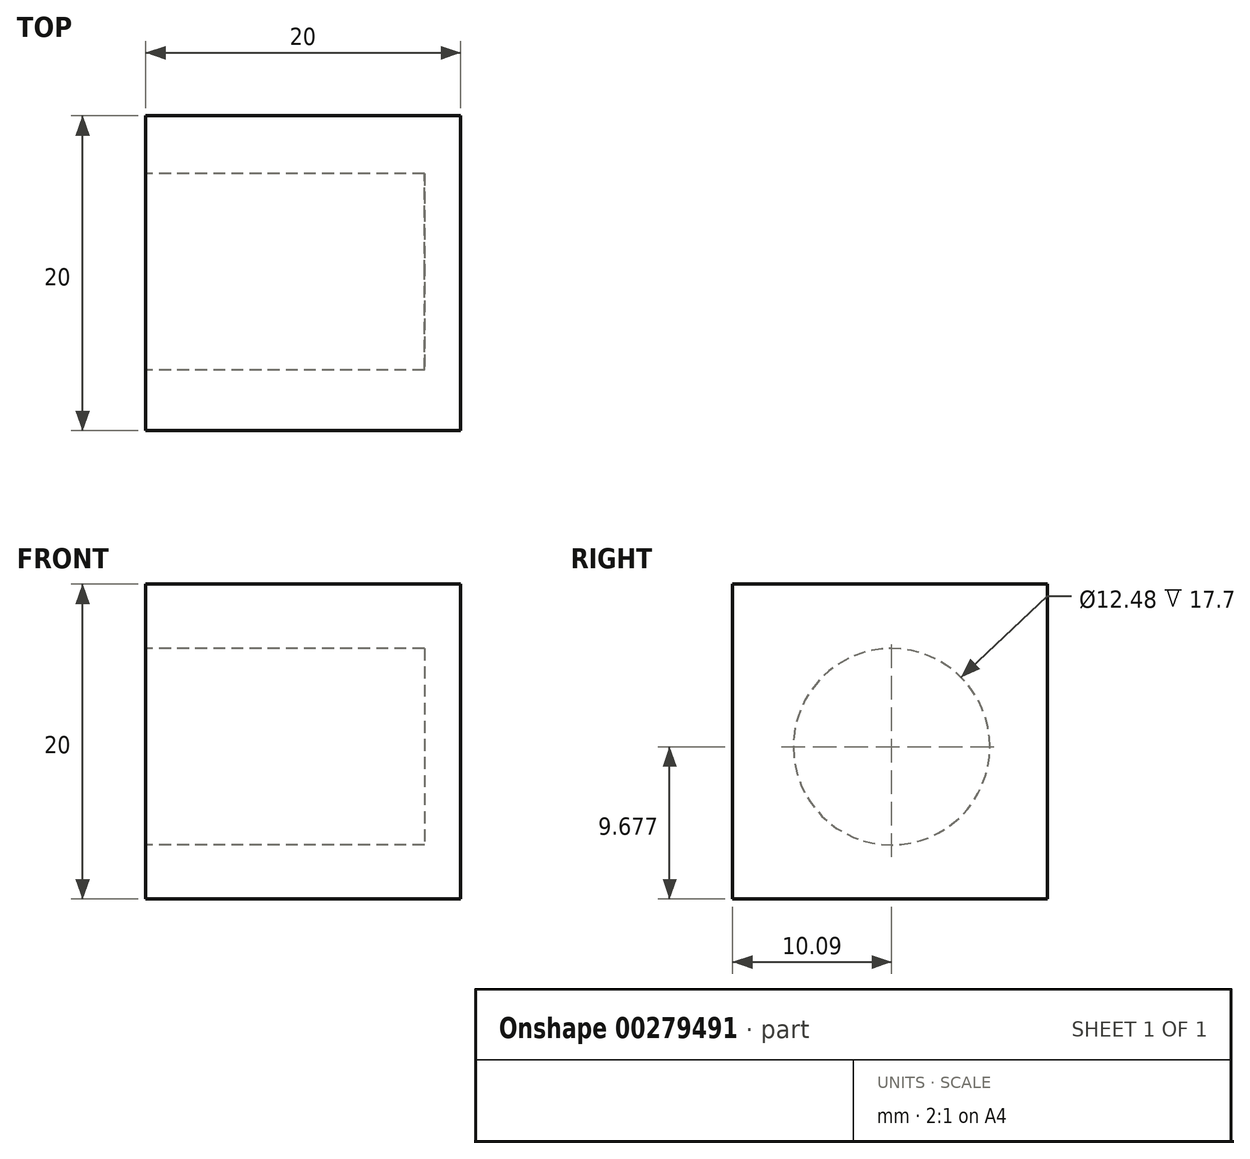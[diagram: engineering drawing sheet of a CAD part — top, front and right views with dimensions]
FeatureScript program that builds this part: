
annotation { "Feature Type Name" : "Feature", "Feature Type Description" : "" }
export const myFeature = defineFeature(function(context is Context, id is Id, definition is map)
    precondition{}
    {
        {
            var Q0;
            Q0=qCreatedBy(makeId("Top.planeOp"),FACE);
            var sketch = newSketch(context, id + "F0", { "sketchPlane" : qUnion([Q0])});
            skLineSegment(sketch, "E0.bottom", {"start": v(0, 0) * mm, "end": v(20, 0) * mm});
            skLineSegment(sketch, "E0.top", {"start": v(0, 20) * mm, "end": v(20, 20) * mm});
            skLineSegment(sketch, "E0.left", {"start": v(0, 0) * mm, "end": v(0, 20) * mm});
            skLineSegment(sketch, "E0.right", {"start": v(20, 0) * mm, "end": v(20, 20) * mm});
            skSolve(sketch);
        }
        {
            var Q0;
            Q0 = qSketchRegion(id + "F0", true);
            extrude(context, id + "F1", {"entities" : qUnion([Q0]), "depth" : 20 * mm});
        }
        {
            var Q0;
            Q0=makeQuery(id+"F1.opExtrude","SWEPT_FACE",FACE,{"disambiguationData":[OSD([sQuery(id+"F0.wireOp",EDGE,"E0.left")])]});
            var sketch = newSketch(context, id + "F2", { "sketchPlane" : qUnion([Q0])});
            skCircle(sketch, "E1", {"center": v(-10.09, 9.68) * mm, "radius": 6.24 * mm});
            skSolve(sketch);
        }
        {
            var Q0;
            Q0 = qSketchRegion(id + "F2", true);
            extrude(context, id + "F3", {"entities" : qUnion([Q0]), "operationType" : NewBodyOperationType.REMOVE, "oppositeDirection" : true, "depth" : 17.7 * mm});
        }
    });
